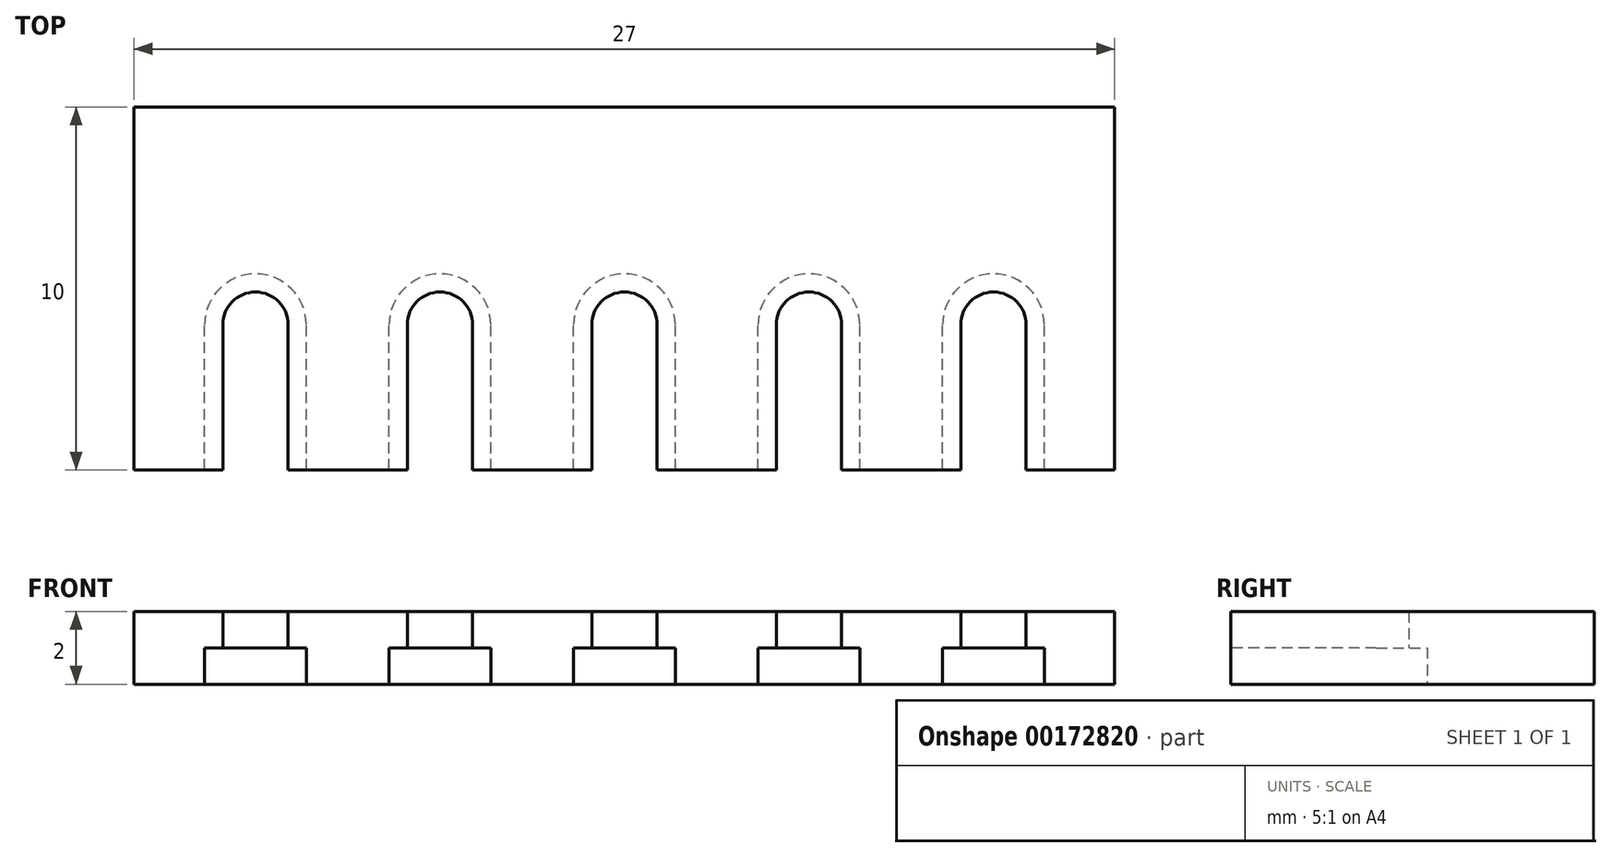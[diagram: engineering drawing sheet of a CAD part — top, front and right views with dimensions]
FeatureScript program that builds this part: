
annotation { "Feature Type Name" : "Feature", "Feature Type Description" : "" }
export const myFeature = defineFeature(function(context is Context, id is Id, definition is map)
    precondition{}
    {
        {
            var Q0;
            Q0=qCreatedBy(makeId("Top.planeOp"),FACE);
            var sketch = newSketch(context, id + "F0", { "sketchPlane" : qUnion([Q0])});
            skLineSegment(sketch, "E0.bottom", {"start": v(-13.5, 5) * mm, "end": v(13.5, 5) * mm});
            skLineSegment(sketch, "E0.top", {"start": v(-13.5, -5) * mm, "end": v(-11.06, -5) * mm});
            skLineSegment(sketch, "E0.left", {"start": v(-13.5, 5) * mm, "end": v(-13.5, -5) * mm});
            skLineSegment(sketch, "E0.right", {"start": v(13.5, 5) * mm, "end": v(13.5, -5) * mm});
            skPoint(sketch, "E0.middle", {"position": v(0, 0) * mm});
            skLineSegment(sketch, "E1.left", {"start": v(-11.06, -5) * mm, "end": v(-11.06, -1) * mm});
            skLineSegment(sketch, "E1.right", {"start": v(-9.26, -5) * mm, "end": v(-9.26, -1) * mm});
            skLineSegment(sketch, "E2.left", {"start": v(-5.98, -5) * mm, "end": v(-5.98, -1) * mm});
            skLineSegment(sketch, "E2.right", {"start": v(-4.18, -5) * mm, "end": v(-4.18, -1) * mm});
            skLineSegment(sketch, "E3.left", {"start": v(4.18, -5) * mm, "end": v(4.18, -1) * mm});
            skLineSegment(sketch, "E3.right", {"start": v(5.98, -5) * mm, "end": v(5.98, -1) * mm});
            skLineSegment(sketch, "E4.left", {"start": v(9.26, -5) * mm, "end": v(9.26, -1) * mm});
            skLineSegment(sketch, "E4.right", {"start": v(11.06, -5) * mm, "end": v(11.06, -1) * mm});
            skArc(sketch, "E5", {"start": v(-9.26, -1) * mm, "mid": v(-10.16, -0.1) * mm, "end": v(-11.06, -1) * mm});
            skArc(sketch, "E6", {"start": v(5.98, -1) * mm, "mid": v(5.08, -0.1) * mm, "end": v(4.18, -1) * mm});
            skArc(sketch, "E7", {"start": v(11.06, -1) * mm, "mid": v(10.16, -0.1) * mm, "end": v(9.26, -1) * mm});
            skLineSegment(sketch, "E8.trimOffspring", {"start": v(11.06, -5) * mm, "end": v(13.5, -5) * mm});
            skLineSegment(sketch, "E9.trimOffspring", {"start": v(5.98, -5) * mm, "end": v(9.26, -5) * mm});
            skLineSegment(sketch, "E10.trimOffspring", {"start": v(-4.18, -5) * mm, "end": v(-0.9, -5) * mm});
            skLineSegment(sketch, "E11.trimOffspring", {"start": v(-9.26, -5) * mm, "end": v(-5.98, -5) * mm});
            skArc(sketch, "E12", {"start": v(-4.18, -1) * mm, "mid": v(-5.08, -0.1) * mm, "end": v(-5.98, -1) * mm});
            skLineSegment(sketch, "E13.left", {"start": v(-0.9, -5) * mm, "end": v(-0.9, -1) * mm});
            skLineSegment(sketch, "E13.right", {"start": v(0.9, -5) * mm, "end": v(0.9, -1) * mm});
            skPoint(sketch, "E13.middle", {"position": v(0, -3) * mm});
            skArc(sketch, "E14", {"start": v(0.9, -1) * mm, "mid": v(0, -0.1) * mm, "end": v(-0.9, -1) * mm});
            skLineSegment(sketch, "E15.trimOffspring", {"start": v(0.9, -5) * mm, "end": v(4.18, -5) * mm});
            skSolve(sketch);
        }
        {
            var Q0;
            Q0 = qSketchRegion(id + "F0", true);
            extrude(context, id + "F1", {"entities" : qUnion([Q0]), "depth" : 2 * mm});
        }
        {
            var Q0;
            Q0=makeQuery(id+"F1.opExtrude","CAP_FACE",FACE,{"disambiguationData":[OSD([sQuery(id+"F0.wireOp",EDGE,"E0.bottom"),sQuery(id+"F0.wireOp",EDGE,"E0.top"),sQuery(id+"F0.wireOp",EDGE,"E0.left"),sQuery(id+"F0.wireOp",EDGE,"E0.right"),sQuery(id+"F0.wireOp",EDGE,"E1.left"),sQuery(id+"F0.wireOp",EDGE,"E1.right"),sQuery(id+"F0.wireOp",EDGE,"E2.left"),sQuery(id+"F0.wireOp",EDGE,"E2.right"),sQuery(id+"F0.wireOp",EDGE,"E3.left"),sQuery(id+"F0.wireOp",EDGE,"E3.right"),sQuery(id+"F0.wireOp",EDGE,"E4.left"),sQuery(id+"F0.wireOp",EDGE,"E4.right"),sQuery(id+"F0.wireOp",EDGE,"E5"),sQuery(id+"F0.wireOp",EDGE,"E6"),sQuery(id+"F0.wireOp",EDGE,"E7"),sQuery(id+"F0.wireOp",EDGE,"E8.trimOffspring"),sQuery(id+"F0.wireOp",EDGE,"E9.trimOffspring"),sQuery(id+"F0.wireOp",EDGE,"E10.trimOffspring"),sQuery(id+"F0.wireOp",EDGE,"E11.trimOffspring"),sQuery(id+"F0.wireOp",EDGE,"E12")])],"isStart":true});
            var sketch = newSketch(context, id + "F2", { "sketchPlane" : qUnion([Q0])});
            skLineSegment(sketch, "E16.0", {"start": v(-11.56, 5) * mm, "end": v(-11.56, 1) * mm});
            skArc(sketch, "E16.1", {"start": v(-8.76, 1) * mm, "mid": v(-10.16, -0.4) * mm, "end": v(-11.56, 1) * mm});
            skLineSegment(sketch, "E16.2", {"start": v(-8.76, 5) * mm, "end": v(-8.76, 1) * mm});
            skLineSegment(sketch, "E17.0", {"start": v(-6.48, 5) * mm, "end": v(-6.48, 1) * mm});
            skArc(sketch, "E17.1", {"start": v(-3.68, 1) * mm, "mid": v(-5.08, -0.4) * mm, "end": v(-6.48, 1) * mm});
            skLineSegment(sketch, "E17.2", {"start": v(-3.68, 5) * mm, "end": v(-3.68, 1) * mm});
            skLineSegment(sketch, "E18.0", {"start": v(3.68, 5) * mm, "end": v(3.68, 1) * mm});
            skArc(sketch, "E18.1", {"start": v(6.48, 1) * mm, "mid": v(5.08, -0.4) * mm, "end": v(3.68, 1) * mm});
            skLineSegment(sketch, "E18.2", {"start": v(6.48, 5) * mm, "end": v(6.48, 1) * mm});
            skLineSegment(sketch, "E19.0", {"start": v(8.76, 5) * mm, "end": v(8.76, 1) * mm});
            skArc(sketch, "E19.1", {"start": v(11.56, 1) * mm, "mid": v(10.16, -0.4) * mm, "end": v(8.76, 1) * mm});
            skLineSegment(sketch, "E19.2", {"start": v(11.56, 5) * mm, "end": v(11.56, 1) * mm});
            skLineSegment(sketch, "E20", {"start": v(-11.56, 5) * mm, "end": v(-11.56, 6.85) * mm});
            skLineSegment(sketch, "E21", {"start": v(11.56, 5) * mm, "end": v(11.56, 6.85) * mm});
            skLineSegment(sketch, "E22", {"start": v(11.56, 6.85) * mm, "end": v(-11.56, 6.85) * mm});
            skLineSegment(sketch, "E23", {"start": v(-8.76, 5) * mm, "end": v(-6.48, 5) * mm});
            skLineSegment(sketch, "E24", {"start": v(6.48, 5) * mm, "end": v(8.76, 5) * mm});
            skLineSegment(sketch, "E25.0", {"start": v(-1.4, 5) * mm, "end": v(-1.4, 1) * mm});
            skArc(sketch, "E25.1", {"start": v(1.4, 1) * mm, "mid": v(0, -0.4) * mm, "end": v(-1.4, 1) * mm});
            skLineSegment(sketch, "E25.2", {"start": v(1.4, 5) * mm, "end": v(1.4, 1) * mm});
            skLineSegment(sketch, "E26", {"start": v(-3.68, 5) * mm, "end": v(-1.4, 5) * mm});
            skLineSegment(sketch, "E27", {"start": v(1.4, 5) * mm, "end": v(3.68, 5) * mm});
            skSolve(sketch);
        }
        {
            var Q0;
            Q0 = qSketchRegion(id + "F2", true);
            extrude(context, id + "F3", {"entities" : qUnion([Q0]), "operationType" : NewBodyOperationType.REMOVE, "oppositeDirection" : true, "depth" : 1 * mm});
        }
    });
